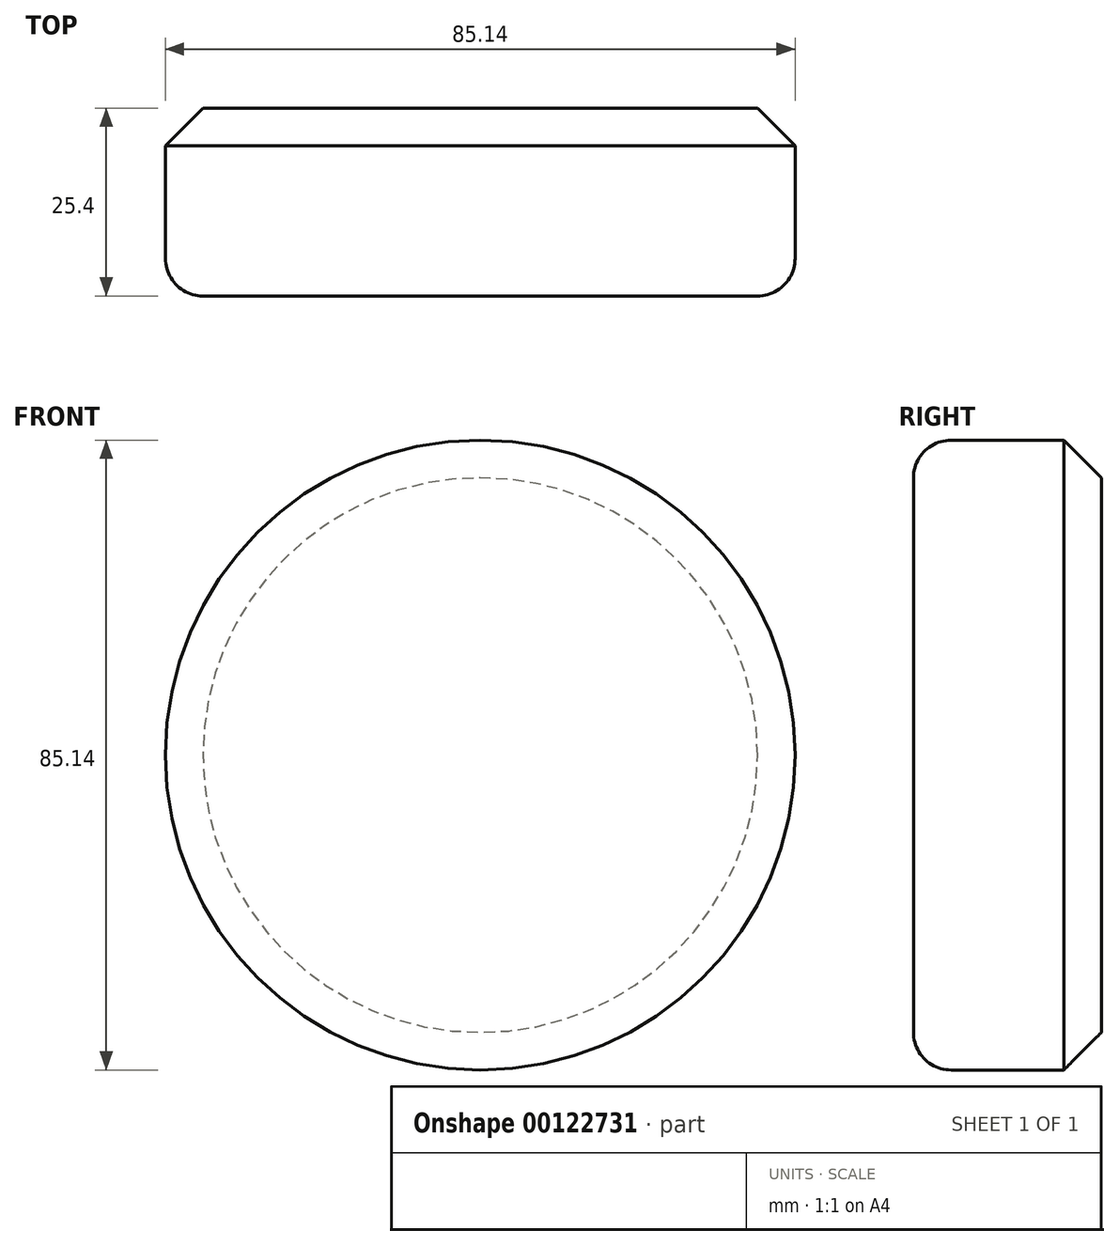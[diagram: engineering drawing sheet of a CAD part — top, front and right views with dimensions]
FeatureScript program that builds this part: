
annotation { "Feature Type Name" : "Feature", "Feature Type Description" : "" }
export const myFeature = defineFeature(function(context is Context, id is Id, definition is map)
    precondition{}
    {
        {
            var Q0;
            Q0=qCreatedBy(makeId("Front.planeOp"),FACE);
            var sketch = newSketch(context, id + "F0", { "sketchPlane" : qUnion([Q0])});
            skCircle(sketch, "E0", {"center": v(0, 0) * mm, "radius": 42.57 * mm});
            skSolve(sketch);
        }
        {
            var Q0;
            Q0=makeQuery(id+"F0.imprint","IMPRINT",FACE,{"disambiguationData":[TD([[makeQuery(id+"F0.imprint","IMPRINT",EDGE,{"derivedFrom":sQuery(id+"F0.wireOp",EDGE,"E0")}),1.0]])]});
            extrude(context, id + "F1", {"entities" : qUnion([Q0]), "depth" : 25.4 * mm});
        }
        {
            var Q0;
            Q0=makeQuery(id+"F1.opExtrude","CAP_EDGE",EDGE,{"disambiguationData":[OSD([sQuery(id+"F0.wireOp",EDGE,"E0")])],"isStart":false});
            fillet(context, id + "F2", {"entities" : qUnion([Q0]), "radius" : 5.08 * mm, "tangentPropagation" : true, "allowEdgeOverflow" : false});
        }
        {
            var Q0;
            Q0=makeQuery(id+"F1.opExtrude","CAP_EDGE",EDGE,{"disambiguationData":[OSD([sQuery(id+"F0.wireOp",EDGE,"E0")])],"isStart":true});
            chamfer(context, id + "F3", {"entities" : qUnion([Q0]), "width" : 5.08 * mm, "tangentPropagation" : true});
        }
    });
